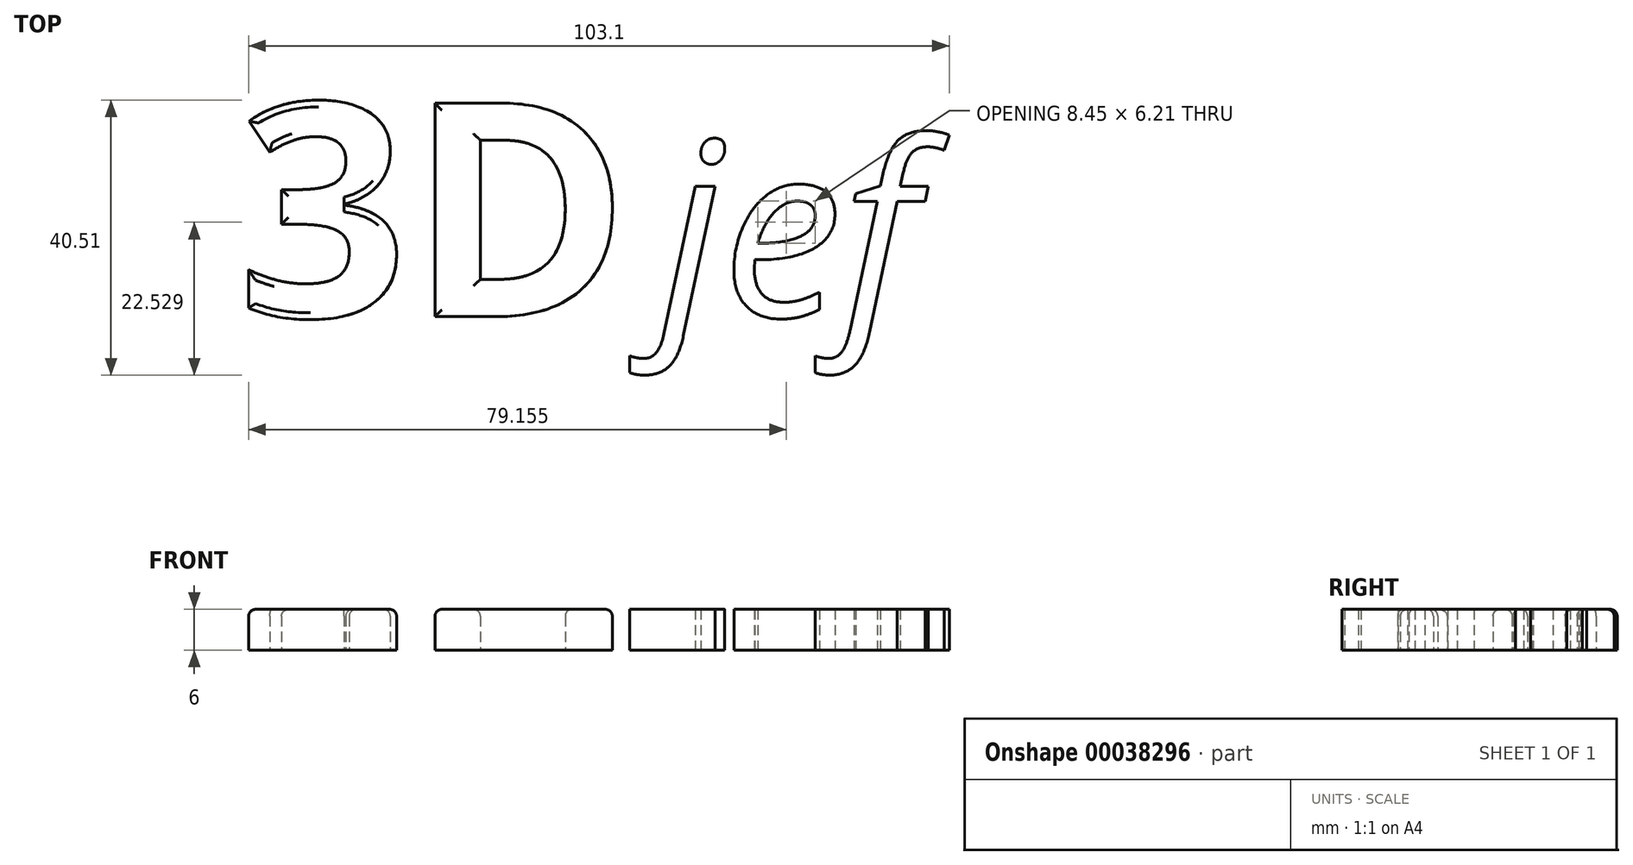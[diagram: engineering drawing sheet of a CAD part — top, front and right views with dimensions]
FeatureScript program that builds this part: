
annotation { "Feature Type Name" : "Feature", "Feature Type Description" : "" }
export const myFeature = defineFeature(function(context is Context, id is Id, definition is map)
    precondition{}
    {
        {
            var Q0;
            Q0=qCreatedBy(makeId("Top.planeOp"),FACE);
            var sketch = newSketch(context, id + "F0", { "sketchPlane" : qUnion([Q0])});
            skText(sketch, "E0", { "text": "3D", "fontName": "OpenSans-Bold.ttf"});
            skText(sketch, "E1", { "text": "jef", "fontName": "OpenSans-Italic.ttf"});
            const initialGuessF0  = {"E0": [-0.0552, 0, 1, 0, 0.03172], "E1": [0.00708, 0, 1, 0, 0.0258]};
            skSetInitialGuess(sketch, initialGuessF0);
            skSolve(sketch);
        }
        {
            var Q0;
            Q0=makeQuery(id+"F0.imprint","IMPRINT",FACE,{"disambiguationData":[TD([[makeQuery(id+"F0.imprint","IMPRINT",EDGE,{"derivedFrom":sQuery(id+"F0.wireOp",EDGE,"E0.sketch_text.stroke-0")}),-1.0]])]});
            var Q1;
            Q1=makeQuery(id+"F0.imprint","IMPRINT",FACE,{"disambiguationData":[TD([[makeQuery(id+"F0.imprint","IMPRINT",EDGE,{"derivedFrom":sQuery(id+"F0.wireOp",EDGE,"E1.sketch_text.stroke-0")}),-1.0]])]});
            var Q2;
            Q2=makeQuery(id+"F0.imprint","IMPRINT",FACE,{"disambiguationData":[TD([[makeQuery(id+"F0.imprint","IMPRINT",EDGE,{"derivedFrom":sQuery(id+"F0.wireOp",EDGE,"E1.sketch_text.stroke-9")}),-1.0]])]});
            var Q3;
            Q3=makeQuery(id+"F0.imprint","IMPRINT",FACE,{"disambiguationData":[TD([[makeQuery(id+"F0.imprint","IMPRINT",EDGE,{"derivedFrom":sQuery(id+"F0.wireOp",EDGE,"E1.sketch_text.stroke-41")}),-1.0]])]});
            var Q4;
            Q4=makeQuery(id+"F0.imprint","IMPRINT",FACE,{"disambiguationData":[TD([[makeQuery(id+"F0.imprint","IMPRINT",EDGE,{"derivedFrom":sQuery(id+"F0.wireOp",EDGE,"E0.sketch_text.stroke-27")}),-1.0]])]});
            var Q5;
            Q5=makeQuery(id+"F0.imprint","IMPRINT",FACE,{"disambiguationData":[TD([[makeQuery(id+"F0.imprint","IMPRINT",EDGE,{"derivedFrom":sQuery(id+"F0.wireOp",EDGE,"E1.sketch_text.stroke-16")}),-1.0]])]});
            extrude(context, id + "F1", {"entities" : qUnion([Q0, Q1, Q2, Q3, Q4, Q5]), "depth" : 6 * mm});
        }
        {
            var Q0;
            Q0=makeQuery(id+"F1.opExtrude","CAP_EDGE",EDGE,{"disambiguationData":[OSD([sQuery(id+"F0.wireOp",EDGE,"E0.sketch_text.stroke-6")])],"isStart":false});
            var Q1;
            Q1=makeQuery(id+"F1.opExtrude","CAP_EDGE",EDGE,{"disambiguationData":[OSD([sQuery(id+"F0.wireOp",EDGE,"E0.sketch_text.stroke-0")])],"isStart":false});
            var Q2;
            Q2=makeQuery(id+"F1.opExtrude","CAP_EDGE",EDGE,{"disambiguationData":[OSD([sQuery(id+"F0.wireOp",EDGE,"E0.sketch_text.stroke-23")])],"isStart":false});
            var Q3;
            Q3=makeQuery(id+"F1.opExtrude","CAP_EDGE",EDGE,{"disambiguationData":[OSD([sQuery(id+"F0.wireOp",EDGE,"E0.sketch_text.stroke-21")])],"isStart":false});
            var Q4;
            Q4=makeQuery(id+"F1.opExtrude","CAP_EDGE",EDGE,{"disambiguationData":[OSD([sQuery(id+"F0.wireOp",EDGE,"E0.sketch_text.stroke-16")])],"isStart":false});
            var Q5;
            Q5=makeQuery(id+"F1.opExtrude","CAP_EDGE",EDGE,{"disambiguationData":[OSD([sQuery(id+"F0.wireOp",EDGE,"E0.sketch_text.stroke-14")])],"isStart":false});
            var Q6;
            Q6=makeQuery(id+"F1.opExtrude","CAP_EDGE",EDGE,{"disambiguationData":[OSD([sQuery(id+"F0.wireOp",EDGE,"E0.sketch_text.stroke-8")])],"isStart":false});
            var Q7;
            Q7=makeQuery(id+"F1.opExtrude","CAP_EDGE",EDGE,{"disambiguationData":[OSD([sQuery(id+"F0.wireOp",EDGE,"E0.sketch_text.stroke-30")])],"isStart":false});
            var Q8;
            Q8=makeQuery(id+"F1.opExtrude","CAP_EDGE",EDGE,{"disambiguationData":[OSD([sQuery(id+"F0.wireOp",EDGE,"E0.sketch_text.stroke-31")])],"isStart":false});
            var Q9;
            Q9=makeQuery(id+"F1.opExtrude","CAP_EDGE",EDGE,{"disambiguationData":[OSD([sQuery(id+"F0.wireOp",EDGE,"E0.sketch_text.stroke-36")])],"isStart":false});
            var Q10;
            Q10=makeQuery(id+"F1.opExtrude","CAP_EDGE",EDGE,{"disambiguationData":[OSD([sQuery(id+"F0.wireOp",EDGE,"E0.sketch_text.stroke-35")])],"isStart":false});
            fillet(context, id + "F2", {"entities" : qUnion([Q0, Q1, Q2, Q3, Q4, Q5, Q6, Q7, Q8, Q9, Q10]), "radius" : 1 * mm, "tangentPropagation" : true, "allowEdgeOverflow" : false});
        }
    });
